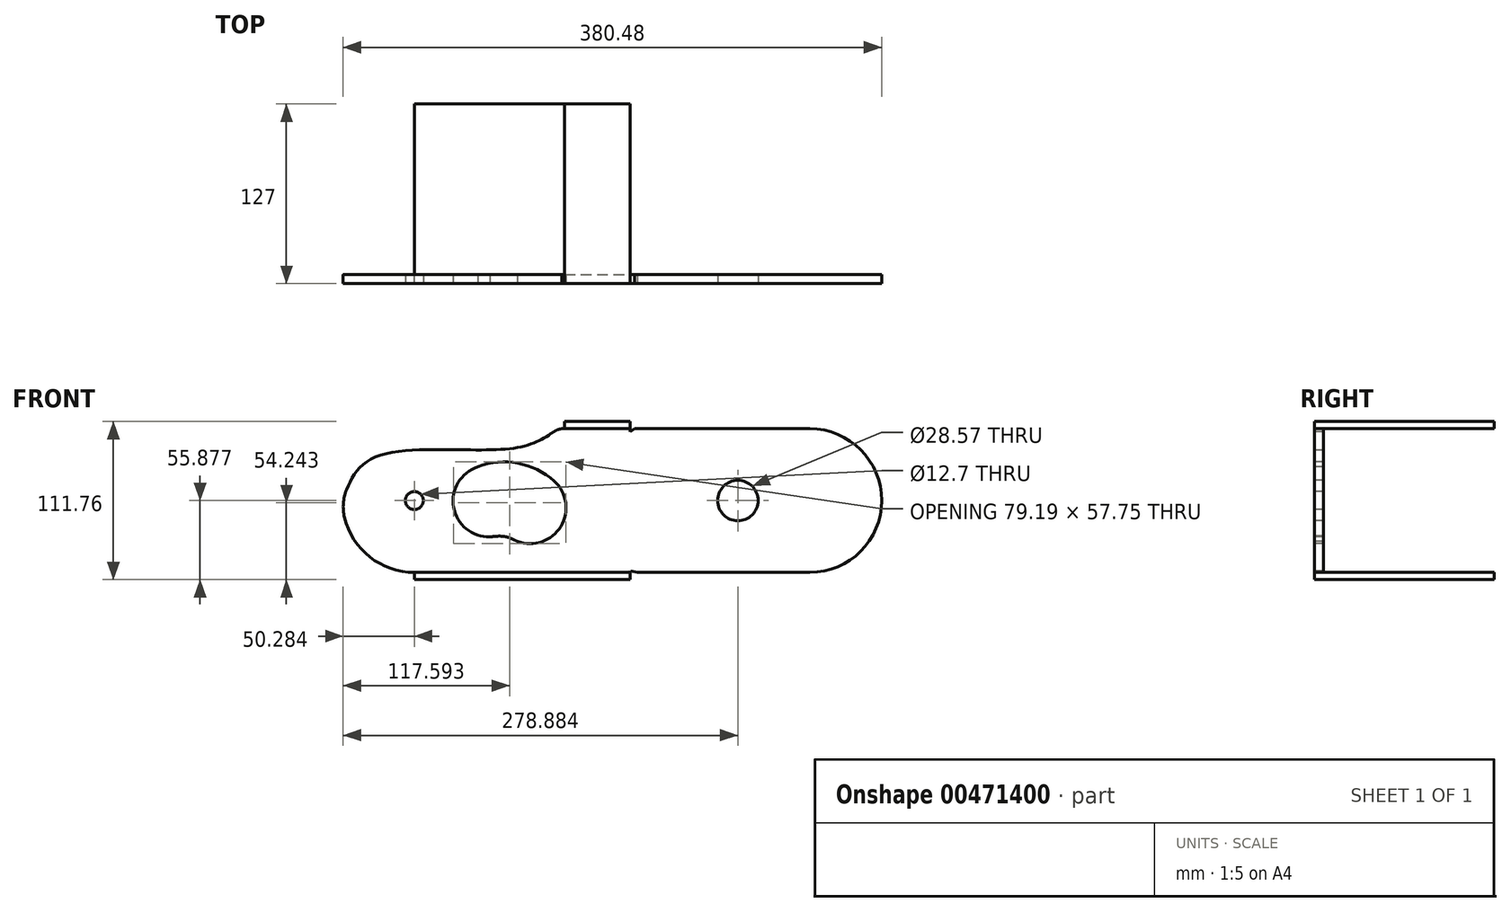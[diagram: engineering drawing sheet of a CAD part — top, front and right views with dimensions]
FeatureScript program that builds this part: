
annotation { "Feature Type Name" : "Feature", "Feature Type Description" : "" }
export const myFeature = defineFeature(function(context is Context, id is Id, definition is map)
    precondition{}
    {
        {
            var Q0;
            Q0=qCreatedBy(makeId("Front.planeOp"),FACE);
            var sketch = newSketch(context, id + "F0", { "sketchPlane" : qUnion([Q0])});
            skLineSegment(sketch, "E0.bottom", {"start": v(3.5, -52.7) * mm, "end": v(178.54, -52.7) * mm});
            skLineSegment(sketch, "E0.top", {"start": v(-100.86, 48.9) * mm, "end": v(178.54, 48.9) * mm});
            skLineSegment(sketch, "E1", {"start": v(-151.66, -1.9) * mm, "end": v(229.34, -1.9) * mm, "construction": true});
            skLineSegment(sketch, "E2", {"start": v(38.84, 48.9) * mm, "end": v(38.84, -52.7) * mm, "construction": true});
            skCircle(sketch, "E3", {"center": v(178.54, -1.9) * mm, "radius": 50.8 * mm});
            skArc(sketch, "E4", {"start": v(-64.87, -37.75) * mm, "mid": v(-81.46, 45.06) * mm, "end": v(-151.66, -1.9) * mm});
            skFitSpline(sketch, "E5", {"points": [v(-151.66, -1.9) * mm, v(-128.36, -32.7) * mm, v(-31.74, -38.78) * mm, v(0.63, -52.7) * mm], "startDerivative": vector(47.43, -131.99) * mm, "endDerivative": vector(91.44, -65.54) * mm});
            skLineSegment(sketch, "E6", {"start": v(-100.86, 48.9) * mm, "end": v(-100.86, -1.9) * mm, "construction": true});
            skLineSegment(sketch, "E7", {"start": v(178.54, 48.9) * mm, "end": v(178.54, -1.9) * mm, "construction": true});
            skLineSegment(sketch, "E8", {"start": v(178.54, -52.7) * mm, "end": v(178.54, -1.9) * mm, "construction": true});
            skPoint(sketch, "E9", {"position": v(-64.87, -37.75) * mm});
            skCircle(sketch, "E10", {"center": v(-100.86, -1.9) * mm, "radius": 6.35 * mm});
            skPoint(sketch, "E11", {"position": v(-37.36, 23.5) * mm});
            skArc(sketch, "E12", {"start": v(-85.7, 48.9) * mm, "mid": v(-86.21, 47.9) * mm, "end": v(-86.7, 46.9) * mm});
            skLineSegment(sketch, "E13", {"start": v(-37.36, 23.5) * mm, "end": v(-0.8, -17.07) * mm, "construction": true});
            skLineSegment(sketch, "E14", {"start": v(-37.36, 23.5) * mm, "end": v(-58.88, -26.68) * mm, "construction": true});
            skPoint(sketch, "E15", {"position": v(-19.08, 3.22) * mm});
            skPoint(sketch, "E16", {"position": v(-48.12, -1.59) * mm});
            skCircle(sketch, "E17", {"center": v(-48.12, -1.59) * mm, "radius": 25.4 * mm});
            skCircle(sketch, "E18", {"center": v(-19.08, 3.22) * mm, "radius": 25.4 * mm});
            skArc(sketch, "E19", {"start": v(-38.1, 21.76) * mm, "mid": v(-37.04, 21.63) * mm, "end": v(-36.08, 22.1) * mm});
            skArc(sketch, "E20", {"start": v(-58.13, -24.93) * mm, "mid": v(-28.75, -28.5) * mm, "end": v(-2.08, -15.65) * mm});
            skFitSpline(sketch, "E21", {"points": [v(-4.43, -49.14) * mm, v(5.3, -52.7) * mm, v(33.1, -36.63) * mm], "startDerivative": vector(23.89, -16.09) * mm, "endDerivative": vector(48.9, 36.33) * mm});
            skCircle(sketch, "E22", {"center": v(127.74, -1.9) * mm, "radius": 14.29 * mm});
            skFitSpline(sketch, "E23", {"points": [v(-47.37, 23.8) * mm, v(-37.36, 23.5) * mm, v(-27.97, 27.01) * mm], "startDerivative": vector(20.35, -2.5) * mm, "endDerivative": vector(18.46, 8.91) * mm});
            skPoint(sketch, "E24", {"position": v(51.54, 48.9) * mm});
            skLineSegment(sketch, "E25", {"start": v(51.54, 48.9) * mm, "end": v(51.95, 47.81) * mm});
            skLineSegment(sketch, "E26", {"start": v(51.95, 47.81) * mm, "end": v(56.55, 48.9) * mm});
            skPoint(sketch, "E27", {"position": v(51.54, -52.7) * mm});
            skLineSegment(sketch, "E28", {"start": v(51.54, -52.7) * mm, "end": v(51.54, -50.5) * mm});
            skLineSegment(sketch, "E29", {"start": v(51.54, -50.5) * mm, "end": v(54.74, -52.7) * mm});
            skSolve(sketch);
        }
        {
            var Q0;
            {var subQ12=sQuery(id+"F0.wireOp",EDGE,"E12");Q0=makeQuery(id+"F0.imprint","IMPRINT",FACE,{"disambiguationData":[TD([[makeQuery(id+"F0.imprint","IMPRINT",EDGE,{"derivedFrom":subQ12}),1.0]])]});}
            var Q1;
            {var subQ0=sQuery(id+"F0.wireOp",EDGE,"E3");var subQ1=makeQuery(id+"F0.imprint","INTERSECT",VERTEX,{"derivedFrom":[sQuery(id+"F0.wireOp",EDGE,"E0.top"),subQ0]});Q1=makeQuery(id+"F0.imprint","IMPRINT",FACE,{"disambiguationData":[TD([[makeQuery(id+"F0.imprint","IMPRINT",EDGE,{"disambiguationData":[TD([[subQ1,-1.0]])],"derivedFrom":subQ0}),1.0]])]});}
            var Q2;
            Q2=makeQuery(id+"F0.imprint","IMPRINT",FACE,{"disambiguationData":[TD([[makeQuery(id+"F0.imprint","IMPRINT",EDGE,{"derivedFrom":sQuery(id+"F0.wireOp",EDGE,"E10")}),-1.0]])]});
            var Q3;
            {var subQ0=sQuery(id+"F0.wireOp",EDGE,"E20");var subQ1=sQuery(id+"F0.wireOp",EDGE,"E4");var subQ2=makeQuery(id+"F0.imprint","INTERSECT",VERTEX,{"derivedFrom":[subQ1,subQ0]});Q3=makeQuery(id+"F0.imprint","IMPRINT",FACE,{"disambiguationData":[TD([[makeQuery(id+"F0.imprint","IMPRINT",EDGE,{"disambiguationData":[TD([[subQ2,-1.0]])],"derivedFrom":subQ1}),1.0]])]});}
            var Q4;
            {var subQ3=sQuery(id+"F0.wireOp",EDGE,"E12");Q4=makeQuery(id+"F0.imprint","IMPRINT",FACE,{"disambiguationData":[TD([[makeQuery(id+"F0.imprint","IMPRINT",EDGE,{"derivedFrom":subQ3}),-1.0]])]});}
            var Q5;
            {var subQ0=sQuery(id+"F0.wireOp",EDGE,"E23");var subQ1=sQuery(id+"F0.wireOp",EDGE,"E18");var subQ2=makeQuery(id+"F0.imprint","INTERSECT",VERTEX,{"disambiguationData":[OD(0.0)],"derivedFrom":[subQ1,subQ0]});Q5=makeQuery(id+"F0.imprint","IMPRINT",FACE,{"disambiguationData":[TD([[makeQuery(id+"F0.imprint","IMPRINT",EDGE,{"disambiguationData":[TD([[subQ2,-1.0]])],"derivedFrom":subQ1}),1.0]])]});}
            var Q6;
            {var subQ0=sQuery(id+"F0.wireOp",EDGE,"E23");var subQ1=sQuery(id+"F0.wireOp",EDGE,"E17");var subQ2=makeQuery(id+"F0.imprint","INTERSECT",VERTEX,{"disambiguationData":[OD(0.0)],"derivedFrom":[subQ1,subQ0]});Q6=makeQuery(id+"F0.imprint","IMPRINT",FACE,{"disambiguationData":[TD([[makeQuery(id+"F0.imprint","IMPRINT",EDGE,{"disambiguationData":[TD([[subQ2,1.0]])],"derivedFrom":subQ1}),1.0]])]});}
            var Q7;
            {var subQ0=sQuery(id+"F0.wireOp",EDGE,"E21");var subQ1=sQuery(id+"F0.wireOp",EDGE,"E0.bottom");var subQ2=makeQuery(id+"F0.imprint","INTERSECT",VERTEX,{"disambiguationData":[OD(0.0)],"derivedFrom":[subQ1,subQ0]});Q7=makeQuery(id+"F0.imprint","IMPRINT",FACE,{"disambiguationData":[TD([[makeQuery(id+"F0.imprint","IMPRINT",EDGE,{"disambiguationData":[TD([[subQ2,-1.0]])],"derivedFrom":subQ1}),-1.0]])]});}
            extrude(context, id + "F1", {"entities" : qUnion([Q0, Q1, Q2, Q3, Q4, Q5, Q6, Q7]), "depth" : 6.35 * mm});
        }
        {
            var Q0;
            Q0=makeQuery(id+"F1.opExtrude","SWEPT_EDGE",EDGE,{"disambiguationData":[OSD([sQuery(id+"F0.wireOp",EDGE,"E4"),sQuery(id+"F0.wireOp",EDGE,"E5")])]});
            fillet(context, id + "F2", {"entities" : qUnion([Q0]), "radius" : 32.03 * mm, "tangentPropagation" : true, "allowEdgeOverflow" : false});
        }
        {
            var Q0;
            Q0=makeQuery(id+"F1.opExtrude","SWEPT_BODY",BODY,{"disambiguationData":[OSD([sQuery(id+"F0.wireOp",EDGE,"E0.bottom"),sQuery(id+"F0.wireOp",EDGE,"E0.top"),sQuery(id+"F0.wireOp",EDGE,"E3"),sQuery(id+"F0.wireOp",EDGE,"E4"),sQuery(id+"F0.wireOp",EDGE,"E5"),sQuery(id+"F0.wireOp",EDGE,"E10"),sQuery(id+"F0.wireOp",EDGE,"E17"),sQuery(id+"F0.wireOp",EDGE,"E18"),sQuery(id+"F0.wireOp",EDGE,"E20"),sQuery(id+"F0.wireOp",EDGE,"E21"),sQuery(id+"F0.wireOp",EDGE,"E22"),sQuery(id+"F0.wireOp",EDGE,"E23")])]});
            var Q1;
            Q1=makeQuery(id+"F1.opExtrude","CAP_EDGE",EDGE,{"disambiguationData":[OSD([sQuery(id+"F0.wireOp",EDGE,"E0.top")])],"isStart":false});
            var Q2;
            {var subQ0=sQuery(id+"F0.wireOp",EDGE,"E0.top");var subQ1=makeQuery(id+"F0.imprint","INTERSECT",VERTEX,{"derivedFrom":[subQ0,sQuery(id+"F0.wireOp",EDGE,"E12")]});Q2=makeQuery(id+"F1.opExtrude","CAP_EDGE",EDGE,{"disambiguationData":[OSD([subQ0]),TDD([makeQuery(id+"F0.imprint","IMPRINT",EDGE,{"disambiguationData":[TD([[makeQuery(id+"F0.imprint","INTERSECT",VERTEX,{"derivedFrom":[subQ0,sQuery(id+"F0.wireOp",EDGE,"E4")]}),-1.0]])],"derivedFrom":subQ0}),makeQuery(id+"F0.imprint","IMPRINT",EDGE,{"disambiguationData":[TD([[subQ1,-1.0]])],"derivedFrom":subQ0})])],"isStart":false});}
            transform(context, id + "F3", {"entities" : qUnion([Q0]), "transformType" : TransformType.ROTATION, "transformAxis" : qUnion([Q2]), "angle" : 180 * degree, "makeCopy" : false});
        }
        {
            var Q0;
            Q0=makeQuery(id+"F1.opExtrude","SWEPT_FACE",FACE,{"disambiguationData":[OSD([sQuery(id+"F0.wireOp",EDGE,"E0.top")])]});
            var sketch = newSketch(context, id + "F4", { "sketchPlane" : qUnion([Q0])});
            skLineSegment(sketch, "E30.bottom", {"start": v(-100.86, 12.7) * mm, "end": v(51.54, 12.7) * mm});
            skLineSegment(sketch, "E30.top", {"start": v(-100.86, -114.3) * mm, "end": v(51.54, -114.3) * mm});
            skLineSegment(sketch, "E30.left", {"start": v(-100.86, 12.7) * mm, "end": v(-100.86, -114.3) * mm});
            skLineSegment(sketch, "E30.right", {"start": v(51.54, 12.7) * mm, "end": v(51.54, -114.3) * mm});
            skSolve(sketch);
        }
        {
            var Q0;
            {var subQ0=sQuery(id+"F4.wireOp",EDGE,"E30.top");Q0=makeQuery(id+"F4.imprint","IMPRINT",FACE,{"disambiguationData":[TD([[makeQuery(id+"F4.imprint","IMPRINT",EDGE,{"derivedFrom":subQ0}),1.0]])]});}
            var Q1;
            {var subQ0=sQuery(id+"F4.wireOp",EDGE,"E30.bottom");Q1=makeQuery(id+"F4.imprint","IMPRINT",FACE,{"disambiguationData":[TD([[makeQuery(id+"F4.imprint","IMPRINT",EDGE,{"derivedFrom":subQ0}),-1.0]])]});}
            extrude(context, id + "F5", {"entities" : qUnion([Q0, Q1]), "depth" : 5.08 * mm});
        }
        {
            var Q0;
            {var subQ0=sQuery(id+"F0.wireOp",EDGE,"E0.bottom");Q0=makeQuery(id+"F1.opExtrude","SWEPT_FACE",FACE,{"disambiguationData":[OSD([subQ0]),TDD([makeQuery(id+"F0.imprint","IMPRINT",EDGE,{"disambiguationData":[TD([[makeQuery(id+"F0.imprint","INTERSECT",VERTEX,{"disambiguationData":[OD(1.0)],"derivedFrom":[subQ0,sQuery(id+"F0.wireOp",EDGE,"E21")]}),-1.0]])],"derivedFrom":subQ0})])]});}
            var sketch = newSketch(context, id + "F6", { "sketchPlane" : qUnion([Q0])});
            skLineSegment(sketch, "E31.bottom", {"start": v(5.3, -12.7) * mm, "end": v(51.54, -12.7) * mm});
            skLineSegment(sketch, "E31.top", {"start": v(5.3, 114.3) * mm, "end": v(51.54, 114.3) * mm});
            skLineSegment(sketch, "E31.left", {"start": v(5.3, -12.7) * mm, "end": v(5.3, 114.3) * mm});
            skLineSegment(sketch, "E31.right", {"start": v(51.54, -12.7) * mm, "end": v(51.54, 114.3) * mm});
            skSolve(sketch);
        }
        {
            var Q0;
            {var subQ0=sQuery(id+"F6.wireOp",EDGE,"E31.top");Q0=makeQuery(id+"F6.imprint","IMPRINT",FACE,{"disambiguationData":[TD([[makeQuery(id+"F6.imprint","IMPRINT",EDGE,{"derivedFrom":subQ0}),-1.0]])]});}
            var Q1;
            {var subQ0=sQuery(id+"F6.wireOp",EDGE,"E31.bottom");Q1=makeQuery(id+"F6.imprint","IMPRINT",FACE,{"disambiguationData":[TD([[makeQuery(id+"F6.imprint","IMPRINT",EDGE,{"derivedFrom":subQ0}),1.0]])]});}
            extrude(context, id + "F7", {"entities" : qUnion([Q0, Q1]), "depth" : 5.08 * mm});
        }
    });
